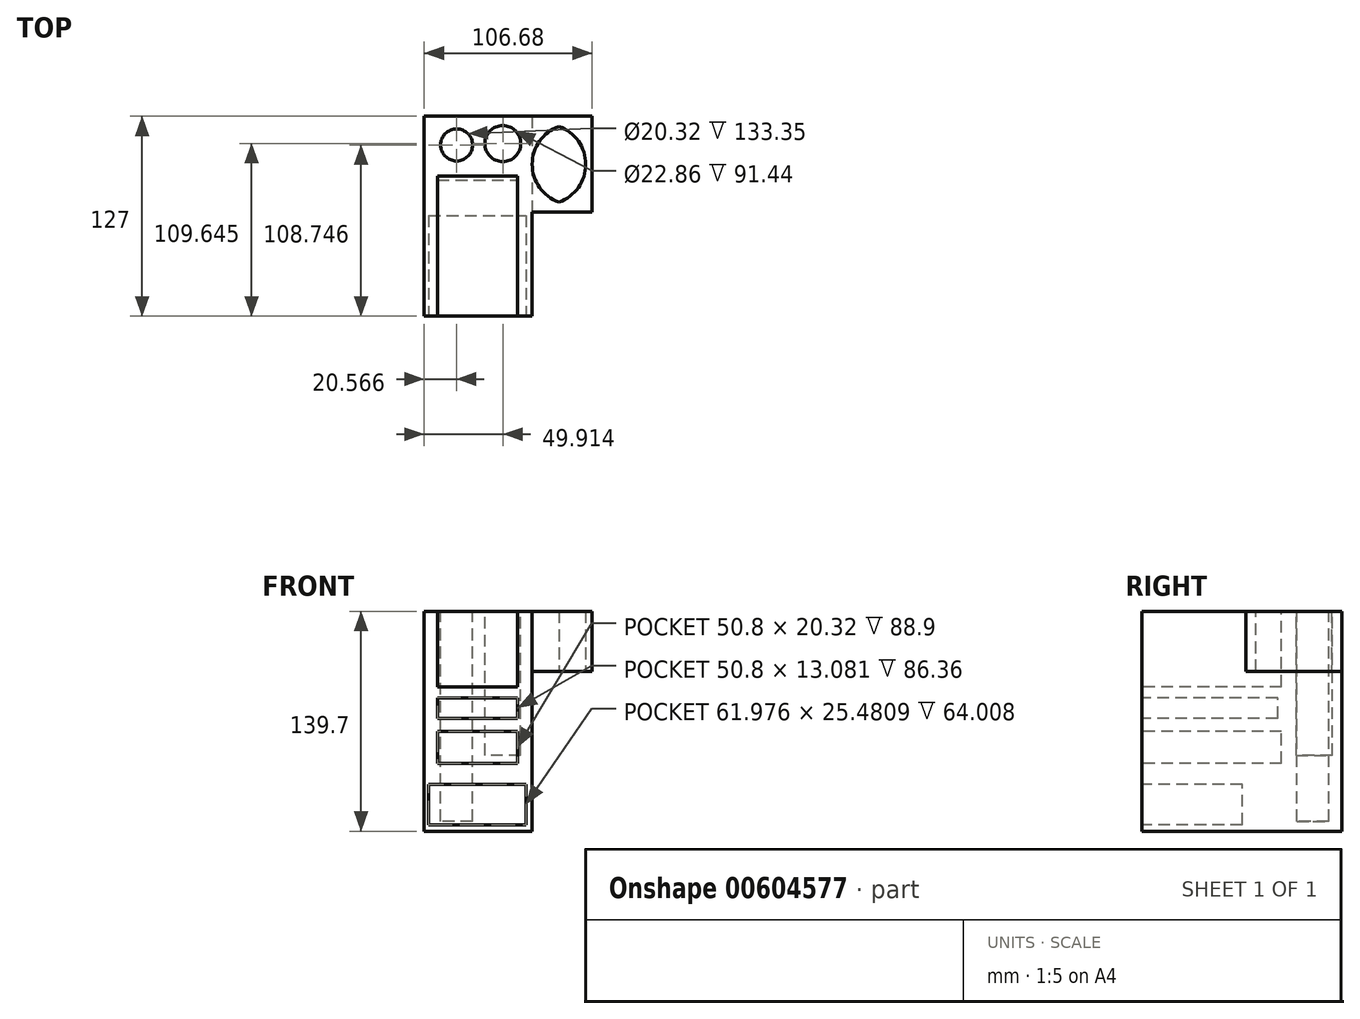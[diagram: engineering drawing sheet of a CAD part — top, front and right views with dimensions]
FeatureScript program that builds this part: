
annotation { "Feature Type Name" : "Feature", "Feature Type Description" : "" }
export const myFeature = defineFeature(function(context is Context, id is Id, definition is map)
    precondition{}
    {
        {
            var Q0;
            Q0=qCreatedBy(makeId("Top.planeOp"),FACE);
            var sketch = newSketch(context, id + "F0", { "sketchPlane" : qUnion([Q0])});
            skLineSegment(sketch, "E0.bottom", {"start": v(0, 0) * mm, "end": v(76.2, 0) * mm});
            skLineSegment(sketch, "E0.top", {"start": v(0, 127) * mm, "end": v(76.2, 127) * mm});
            skLineSegment(sketch, "E0.left", {"start": v(0, 0) * mm, "end": v(0, 127) * mm});
            skLineSegment(sketch, "E0.right", {"start": v(76.2, 0) * mm, "end": v(76.2, 127) * mm});
            skSolve(sketch);
        }
        {
            var Q0;
            Q0=makeQuery(id+"F0.imprint","IMPRINT",FACE,{"disambiguationData":[TD([[makeQuery(id+"F0.imprint","IMPRINT",EDGE,{"derivedFrom":sQuery(id+"F0.wireOp",EDGE,"E0.bottom")}),1.0]])]});
            extrude(context, id + "F1", {"entities" : qUnion([Q0]), "depth" : 139.7 * mm, "offsetDistance" : 25.4 * mm});
        }
        {
            var Q0;
            Q0=makeQuery(id+"F1.opExtrude","CAP_FACE",FACE,{"disambiguationData":[OSD([sQuery(id+"F0.wireOp",EDGE,"E0.bottom"),sQuery(id+"F0.wireOp",EDGE,"E0.top"),sQuery(id+"F0.wireOp",EDGE,"E0.left"),sQuery(id+"F0.wireOp",EDGE,"E0.right")])],"isStart":false});
            var sketch = newSketch(context, id + "F2", { "sketchPlane" : qUnion([Q0])});
            skCircle(sketch, "E1", {"center": v(18.57, 17.6) * mm, "radius": 11.43 * mm});
            skSolve(sketch);
        }
        {
            var Q0;
            Q0=makeQuery(id+"F2.imprint","IMPRINT",FACE,{"disambiguationData":[TD([[makeQuery(id+"F2.imprint","IMPRINT",EDGE,{"derivedFrom":sQuery(id+"F2.wireOp",EDGE,"E1")}),1.0]])]});
            extrude(context, id + "F3", {"entities" : qUnion([Q0]), "operationType" : NewBodyOperationType.REMOVE, "oppositeDirection" : true, "depth" : 91.44 * mm, "offsetDistance" : 25.4 * mm});
        }
        {
            var Q0;
            Q0=makeQuery(id+"F1.opExtrude","CAP_FACE",FACE,{"disambiguationData":[OSD([sQuery(id+"F0.wireOp",EDGE,"E0.bottom"),sQuery(id+"F0.wireOp",EDGE,"E0.top"),sQuery(id+"F0.wireOp",EDGE,"E0.left"),sQuery(id+"F0.wireOp",EDGE,"E0.right")])],"isStart":false});
            var sketch = newSketch(context, id + "F4", { "sketchPlane" : qUnion([Q0])});
            skCircle(sketch, "E2", {"center": v(20.57, 108.75) * mm, "radius": 10.16 * mm});
            skSolve(sketch);
        }
        {
            var Q0;
            Q0=makeQuery(id+"F4.imprint","IMPRINT",FACE,{"disambiguationData":[TD([[makeQuery(id+"F4.imprint","IMPRINT",EDGE,{"derivedFrom":sQuery(id+"F4.wireOp",EDGE,"E2")}),1.0]])]});
            extrude(context, id + "F5", {"entities" : qUnion([Q0]), "operationType" : NewBodyOperationType.REMOVE, "oppositeDirection" : true, "depth" : 133.35 * mm, "offsetDistance" : 25.4 * mm});
        }
        {
            var Q0;
            Q0=makeQuery(id+"F1.opExtrude","SWEPT_FACE",FACE,{"disambiguationData":[OSD([sQuery(id+"F0.wireOp",EDGE,"E0.right")])]});
            extrude(context, id + "F6", {"entities" : qUnion([Q0]), "operationType" : NewBodyOperationType.REMOVE, "oppositeDirection" : true, "depth" : 12.7 * mm, "offsetDistance" : 25.4 * mm});
        }
        {
            var Q0;
            Q0=makeQuery(id+"F1.opExtrude","SWEPT_FACE",FACE,{"disambiguationData":[OSD([sQuery(id+"F0.wireOp",EDGE,"E0.bottom")])]});
            var sketch = newSketch(context, id + "F7", { "sketchPlane" : qUnion([Q0])});
            skLineSegment(sketch, "E3.bottom", {"start": v(3.35, 4.2) * mm, "end": v(64.3, 4.2) * mm});
            skLineSegment(sketch, "E3.top", {"start": v(3.35, 29.68) * mm, "end": v(64.3, 29.68) * mm});
            skLineSegment(sketch, "E3.left", {"start": v(3.35, 4.2) * mm, "end": v(3.35, 29.68) * mm});
            skLineSegment(sketch, "E3.right", {"start": v(64.3, 4.2) * mm, "end": v(64.3, 29.68) * mm});
            skSolve(sketch);
        }
        {
            var Q0;
            Q0=makeQuery(id+"F6.boolean.opBoolean","COPY",FACE,{"derivedFrom":makeQuery(id+"F6.opExtrude","CAP_FACE",FACE,{"disambiguationData":[OSD([sQuery(id+"F0.wireOp",EDGE,"E0.right")])],"isStart":false})});
            extrude(context, id + "F8", {"entities" : qUnion([Q0]), "operationType" : NewBodyOperationType.ADD, "depth" : 5.08 * mm, "offsetDistance" : 25.4 * mm});
        }
        {
            var Q0;
            {var subQ0=sQuery(id+"F7.wireOp",EDGE,"E3.left");Q0=makeQuery(id+"F7.imprint","IMPRINT",FACE,{"disambiguationData":[TD([[makeQuery(id+"F7.imprint","IMPRINT",EDGE,{"derivedFrom":subQ0}),-1.0]])]});}
            var Q1;
            {var subQ0=sQuery(id+"F7.wireOp",EDGE,"E3.right");Q1=makeQuery(id+"F7.imprint","IMPRINT",FACE,{"disambiguationData":[TD([[makeQuery(id+"F7.imprint","IMPRINT",EDGE,{"derivedFrom":subQ0}),1.0]])]});}
            extrude(context, id + "F9", {"entities" : qUnion([Q0, Q1]), "operationType" : NewBodyOperationType.REMOVE, "oppositeDirection" : true, "depth" : 63.5 * mm, "offsetDistance" : 25.4 * mm});
        }
        {
            var Q0;
            Q0=makeQuery(id+"F3.boolean.opBoolean","COPY",FACE,{"derivedFrom":makeQuery(id+"F3.opExtrude","CAP_FACE",FACE,{"disambiguationData":[OSD([sQuery(id+"F2.wireOp",EDGE,"E1")])],"isStart":false})});
            extrude(context, id + "F10", {"entities" : qUnion([Q0]), "operationType" : NewBodyOperationType.ADD, "depth" : 91.44 * mm, "offsetDistance" : 25.4 * mm});
        }
        {
            var Q0;
            {var subQ0=sQuery(id+"F0.wireOp",EDGE,"E0.right");Q0=makeQuery(id+"F10.boolean.opBoolean","MERGE",FACE,{"derivedFrom":[makeQuery(id+"F8.boolean.opBoolean","MERGE",FACE,{"derivedFrom":[makeQuery(id+"F1.opExtrude","CAP_FACE",FACE,{"disambiguationData":[OSD([sQuery(id+"F0.wireOp",EDGE,"E0.bottom"),sQuery(id+"F0.wireOp",EDGE,"E0.top"),sQuery(id+"F0.wireOp",EDGE,"E0.left"),subQ0])],"isStart":false}),makeQuery(id+"F8.opExtrude","SWEPT_FACE",FACE,{"disambiguationData":[OSD([subQ0]),TDD([makeQuery(id+"F6.boolean.opBoolean","COPY",EDGE,{"derivedFrom":makeQuery(id+"F6.opExtrude","CAP_EDGE",EDGE,{"disambiguationData":[OSD([subQ0]),TDD([makeQuery(id+"F1.opExtrude","CAP_EDGE",EDGE,{"disambiguationData":[OSD([subQ0])],"isStart":false})])],"isStart":false})})])]})]}),makeQuery(id+"F10.opExtrude","CAP_FACE",FACE,{"disambiguationData":[OSD([sQuery(id+"F2.wireOp",EDGE,"E1")])],"isStart":false})]});}
            var sketch = newSketch(context, id + "F11", { "sketchPlane" : qUnion([Q0])});
            skCircle(sketch, "E4", {"center": v(49.91, 109.65) * mm, "radius": 11.43 * mm});
            skSolve(sketch);
        }
        {
            var Q0;
            Q0=makeQuery(id+"F11.imprint","IMPRINT",FACE,{"disambiguationData":[TD([[makeQuery(id+"F11.imprint","IMPRINT",EDGE,{"derivedFrom":sQuery(id+"F11.wireOp",EDGE,"E4")}),1.0]])]});
            extrude(context, id + "F12", {"entities" : qUnion([Q0]), "operationType" : NewBodyOperationType.REMOVE, "oppositeDirection" : true, "depth" : 91.44 * mm, "offsetDistance" : 25.4 * mm});
        }
        {
            var Q0;
            {var subQ0=sQuery(id+"F0.wireOp",EDGE,"E0.bottom");Q0=makeQuery(id+"F8.boolean.opBoolean","MERGE",FACE,{"derivedFrom":[makeQuery(id+"F1.opExtrude","SWEPT_FACE",FACE,{"disambiguationData":[OSD([subQ0])]}),makeQuery(id+"F8.opExtrude","SWEPT_FACE",FACE,{"disambiguationData":[OSD([subQ0,sQuery(id+"F0.wireOp",EDGE,"E0.right")])]})]});}
            var sketch = newSketch(context, id + "F13", { "sketchPlane" : qUnion([Q0])});
            skLineSegment(sketch, "E5.bottom", {"start": v(3.35, 43.16) * mm, "end": v(64.3, 43.16) * mm});
            skLineSegment(sketch, "E5.top", {"start": v(3.35, 63.48) * mm, "end": v(64.3, 63.48) * mm});
            skLineSegment(sketch, "E5.left", {"start": v(3.35, 43.16) * mm, "end": v(3.35, 63.48) * mm});
            skLineSegment(sketch, "E5.right", {"start": v(64.3, 43.16) * mm, "end": v(64.3, 63.48) * mm});
            skSolve(sketch);
        }
        {
            var Q0;
            Q0=makeQuery(id+"F13.imprint","IMPRINT",FACE,{"disambiguationData":[TD([[makeQuery(id+"F13.imprint","IMPRINT",EDGE,{"derivedFrom":sQuery(id+"F13.wireOp",EDGE,"E5.bottom")}),1.0]])]});
            extrude(context, id + "F14", {"entities" : qUnion([Q0]), "operationType" : NewBodyOperationType.REMOVE, "oppositeDirection" : true, "depth" : 88.9 * mm, "offsetDistance" : 25.4 * mm});
        }
        {
            var Q0;
            Q0=makeQuery(id+"F14.boolean.opBoolean","COPY",FACE,{"derivedFrom":makeQuery(id+"F14.opExtrude","SWEPT_FACE",FACE,{"disambiguationData":[OSD([sQuery(id+"F13.wireOp",EDGE,"E5.left")])]})});
            extrude(context, id + "F15", {"entities" : qUnion([Q0]), "operationType" : NewBodyOperationType.ADD, "depth" : 5.08 * mm, "offsetDistance" : 25.4 * mm});
        }
        {
            var Q0;
            Q0=makeQuery(id+"F14.boolean.opBoolean","COPY",FACE,{"derivedFrom":makeQuery(id+"F14.opExtrude","SWEPT_FACE",FACE,{"disambiguationData":[OSD([sQuery(id+"F13.wireOp",EDGE,"E5.right")])]})});
            extrude(context, id + "F16", {"entities" : qUnion([Q0]), "operationType" : NewBodyOperationType.ADD, "depth" : 5.08 * mm, "offsetDistance" : 25.4 * mm});
        }
        {
            var Q0;
            {var subQ0=sQuery(id+"F13.wireOp",EDGE,"E5.right");var subQ1=sQuery(id+"F13.wireOp",EDGE,"E5.left");var subQ2=sQuery(id+"F0.wireOp",EDGE,"E0.bottom");Q0=makeQuery(id+"F16.boolean.opBoolean","MERGE",FACE,{"derivedFrom":[makeQuery(id+"F15.boolean.opBoolean","MERGE",FACE,{"derivedFrom":[makeQuery(id+"F8.boolean.opBoolean","MERGE",FACE,{"derivedFrom":[makeQuery(id+"F1.opExtrude","SWEPT_FACE",FACE,{"disambiguationData":[OSD([subQ2])]}),makeQuery(id+"F8.opExtrude","SWEPT_FACE",FACE,{"disambiguationData":[OSD([subQ2,sQuery(id+"F0.wireOp",EDGE,"E0.right")])]})]}),makeQuery(id+"F15.opExtrude","SWEPT_FACE",FACE,{"disambiguationData":[OSD([subQ1]),TDD([makeQuery(id+"F14.boolean.opBoolean","COPY",EDGE,{"derivedFrom":makeQuery(id+"F14.opExtrude","CAP_EDGE",EDGE,{"disambiguationData":[OSD([subQ1])],"isStart":true})})])]})]}),makeQuery(id+"F16.opExtrude","SWEPT_FACE",FACE,{"disambiguationData":[OSD([subQ0]),TDD([makeQuery(id+"F14.boolean.opBoolean","COPY",EDGE,{"derivedFrom":makeQuery(id+"F14.opExtrude","CAP_EDGE",EDGE,{"disambiguationData":[OSD([subQ0])],"isStart":true})})])]})]});}
            var sketch = newSketch(context, id + "F17", { "sketchPlane" : qUnion([Q0])});
            skLineSegment(sketch, "E6.bottom", {"start": v(8.43, 71.79) * mm, "end": v(59.23, 71.79) * mm});
            skLineSegment(sketch, "E6.top", {"start": v(8.43, 84.49) * mm, "end": v(59.23, 84.49) * mm});
            skLineSegment(sketch, "E6.left", {"start": v(8.43, 71.79) * mm, "end": v(8.43, 84.49) * mm});
            skLineSegment(sketch, "E6.right", {"start": v(59.23, 71.79) * mm, "end": v(59.23, 84.49) * mm});
            skSolve(sketch);
        }
        {
            var Q0;
            Q0=makeQuery(id+"F17.imprint","IMPRINT",FACE,{"disambiguationData":[TD([[makeQuery(id+"F17.imprint","IMPRINT",EDGE,{"derivedFrom":sQuery(id+"F17.wireOp",EDGE,"E6.bottom")}),1.0]])]});
            extrude(context, id + "F18", {"entities" : qUnion([Q0]), "operationType" : NewBodyOperationType.REMOVE, "oppositeDirection" : true, "depth" : 86.36 * mm, "offsetDistance" : 25.4 * mm});
        }
        {
            var Q0;
            {var subQ0=sQuery(id+"F13.wireOp",EDGE,"E5.right");var subQ1=sQuery(id+"F13.wireOp",EDGE,"E5.left");var subQ2=sQuery(id+"F0.wireOp",EDGE,"E0.bottom");Q0=makeQuery(id+"F16.boolean.opBoolean","MERGE",FACE,{"derivedFrom":[makeQuery(id+"F15.boolean.opBoolean","MERGE",FACE,{"derivedFrom":[makeQuery(id+"F8.boolean.opBoolean","MERGE",FACE,{"derivedFrom":[makeQuery(id+"F1.opExtrude","SWEPT_FACE",FACE,{"disambiguationData":[OSD([subQ2])]}),makeQuery(id+"F8.opExtrude","SWEPT_FACE",FACE,{"disambiguationData":[OSD([subQ2,sQuery(id+"F0.wireOp",EDGE,"E0.right")])]})]}),makeQuery(id+"F15.opExtrude","SWEPT_FACE",FACE,{"disambiguationData":[OSD([subQ1]),TDD([makeQuery(id+"F14.boolean.opBoolean","COPY",EDGE,{"derivedFrom":makeQuery(id+"F14.opExtrude","CAP_EDGE",EDGE,{"disambiguationData":[OSD([subQ1])],"isStart":true})})])]})]}),makeQuery(id+"F16.opExtrude","SWEPT_FACE",FACE,{"disambiguationData":[OSD([subQ0]),TDD([makeQuery(id+"F14.boolean.opBoolean","COPY",EDGE,{"derivedFrom":makeQuery(id+"F14.opExtrude","CAP_EDGE",EDGE,{"disambiguationData":[OSD([subQ0])],"isStart":true})})])]})]});}
            var sketch = newSketch(context, id + "F19", { "sketchPlane" : qUnion([Q0])});
            skLineSegment(sketch, "E7.bottom", {"start": v(8.43, 91.68) * mm, "end": v(59.23, 91.68) * mm});
            skLineSegment(sketch, "E7.top", {"start": v(8.43, 139.7) * mm, "end": v(59.23, 139.7) * mm});
            skLineSegment(sketch, "E7.left", {"start": v(8.43, 91.68) * mm, "end": v(8.43, 139.7) * mm});
            skLineSegment(sketch, "E7.right", {"start": v(59.23, 91.68) * mm, "end": v(59.23, 139.7) * mm});
            skSolve(sketch);
        }
        {
            var Q0;
            Q0=makeQuery(id+"F19.imprint","IMPRINT",FACE,{"disambiguationData":[TD([[makeQuery(id+"F19.imprint","IMPRINT",EDGE,{"derivedFrom":sQuery(id+"F19.wireOp",EDGE,"E7.bottom")}),1.0]])]});
            extrude(context, id + "F20", {"entities" : qUnion([Q0]), "operationType" : NewBodyOperationType.REMOVE, "oppositeDirection" : true, "depth" : 88.9 * mm, "offsetDistance" : 25.4 * mm});
        }
        {
            var Q0;
            Q0=makeQuery(id+"F20.boolean.opBoolean","COPY",FACE,{"derivedFrom":makeQuery(id+"F20.opExtrude","SWEPT_FACE",FACE,{"disambiguationData":[OSD([sQuery(id+"F19.wireOp",EDGE,"E7.left")])]})});
            var sketch = newSketch(context, id + "F21", { "sketchPlane" : qUnion([Q0])});
            skLineSegment(sketch, "E8.bottom", {"start": v(0, 91.68) * mm, "end": v(6.76, 91.68) * mm});
            skLineSegment(sketch, "E8.top", {"start": v(0, 139.7) * mm, "end": v(6.76, 139.7) * mm});
            skLineSegment(sketch, "E8.left", {"start": v(0, 91.68) * mm, "end": v(0, 139.7) * mm});
            skLineSegment(sketch, "E8.right", {"start": v(6.76, 91.68) * mm, "end": v(6.76, 139.7) * mm});
            skSolve(sketch);
        }
        {
            var Q0;
            Q0=makeQuery(id+"F21.imprint","IMPRINT",FACE,{"disambiguationData":[TD([[makeQuery(id+"F21.imprint","IMPRINT",EDGE,{"derivedFrom":sQuery(id+"F21.wireOp",EDGE,"E8.bottom")}),-1.0]])]});
            extrude(context, id + "F22", {"entities" : qUnion([Q0]), "operationType" : NewBodyOperationType.ADD, "depth" : 55.88 * mm, "offsetDistance" : 25.4 * mm});
        }
        {
            var Q0;
            Q0=makeQuery(id+"F8.opExtrude","CAP_FACE",FACE,{"disambiguationData":[OSD([sQuery(id+"F0.wireOp",EDGE,"E0.right")])],"isStart":false});
            var sketch = newSketch(context, id + "F23", { "sketchPlane" : qUnion([Q0])});
            skLineSegment(sketch, "E9.bottom", {"start": v(127, 139.7) * mm, "end": v(66.04, 139.7) * mm});
            skLineSegment(sketch, "E9.top", {"start": v(127, 101.6) * mm, "end": v(66.04, 101.6) * mm});
            skLineSegment(sketch, "E9.left", {"start": v(127, 139.7) * mm, "end": v(127, 101.6) * mm});
            skLineSegment(sketch, "E9.right", {"start": v(66.04, 139.7) * mm, "end": v(66.04, 101.6) * mm});
            skSolve(sketch);
        }
        {
            var Q0;
            Q0=makeQuery(id+"F23.imprint","IMPRINT",FACE,{"disambiguationData":[TD([[makeQuery(id+"F23.imprint","IMPRINT",EDGE,{"derivedFrom":sQuery(id+"F23.wireOp",EDGE,"E9.bottom")}),-1.0]])]});
            extrude(context, id + "F24", {"entities" : qUnion([Q0]), "operationType" : NewBodyOperationType.ADD, "depth" : 38.1 * mm, "offsetDistance" : 25.4 * mm});
        }
        {
            var Q0;
            Q0=makeQuery(id+"F24.opExtrude","SWEPT_FACE",FACE,{"disambiguationData":[OSD([sQuery(id+"F23.wireOp",EDGE,"E9.top")])]});
            var sketch = newSketch(context, id + "F25", { "sketchPlane" : qUnion([Q0])});
            skLineSegment(sketch, "E10.bottom", {"start": v(68.58, -71.05) * mm, "end": v(102.6, -71.05) * mm});
            skLineSegment(sketch, "E10.top", {"start": v(68.58, -121.88) * mm, "end": v(102.6, -121.88) * mm});
            skLineSegment(sketch, "E10.left", {"start": v(68.58, -71.05) * mm, "end": v(68.58, -121.88) * mm});
            skLineSegment(sketch, "E10.right", {"start": v(102.6, -71.05) * mm, "end": v(102.6, -121.88) * mm});
            skSolve(sketch);
        }
        {
            var Q0;
            Q0=makeQuery(id+"F25.imprint","IMPRINT",FACE,{"disambiguationData":[TD([[makeQuery(id+"F25.imprint","IMPRINT",EDGE,{"derivedFrom":sQuery(id+"F25.wireOp",EDGE,"E10.bottom")}),-1.0]])]});
            extrude(context, id + "F26", {"entities" : qUnion([Q0]), "operationType" : NewBodyOperationType.REMOVE, "oppositeDirection" : true, "depth" : 50.8 * mm, "offsetDistance" : 25.4 * mm});
        }
        {
            var Q0;
            Q0=makeQuery(id+"F26.boolean.opBoolean","COPY",EDGE,{"derivedFrom":makeQuery(id+"F26.opExtrude","SWEPT_EDGE",EDGE,{"disambiguationData":[OSD([sQuery(id+"F25.wireOp",EDGE,"E10.bottom"),sQuery(id+"F25.wireOp",EDGE,"E10.right")])]})});
            var Q1;
            Q1=makeQuery(id+"F26.boolean.opBoolean","COPY",EDGE,{"derivedFrom":makeQuery(id+"F26.opExtrude","SWEPT_EDGE",EDGE,{"disambiguationData":[OSD([sQuery(id+"F25.wireOp",EDGE,"E10.top"),sQuery(id+"F25.wireOp",EDGE,"E10.right")])]})});
            var Q2;
            Q2=makeQuery(id+"F26.boolean.opBoolean","COPY",EDGE,{"derivedFrom":makeQuery(id+"F26.opExtrude","SWEPT_EDGE",EDGE,{"disambiguationData":[OSD([sQuery(id+"F23.wireOp",EDGE,"E9.top"),sQuery(id+"F25.wireOp",EDGE,"E10.bottom"),sQuery(id+"F25.wireOp",EDGE,"E10.left")])]})});
            var Q3;
            Q3=makeQuery(id+"F26.boolean.opBoolean","COPY",EDGE,{"derivedFrom":makeQuery(id+"F26.opExtrude","SWEPT_EDGE",EDGE,{"disambiguationData":[OSD([sQuery(id+"F23.wireOp",EDGE,"E9.top"),sQuery(id+"F25.wireOp",EDGE,"E10.top"),sQuery(id+"F25.wireOp",EDGE,"E10.left")])]})});
            fillet(context, id + "F27", {"entities" : qUnion([Q0, Q1, Q2, Q3]), "radius" : 25.4 * mm, "tangentPropagation" : true, "allowEdgeOverflow" : false});
        }
        {
            var Q0;
            Q0=makeQuery(id+"F9.boolean.opBoolean","COPY",FACE,{"derivedFrom":makeQuery(id+"F9.opExtrude","CAP_FACE",FACE,{"disambiguationData":[OSD([sQuery(id+"F7.wireOp",EDGE,"E3.bottom"),sQuery(id+"F7.wireOp",EDGE,"E3.top"),sQuery(id+"F7.wireOp",EDGE,"E3.left"),sQuery(id+"F7.wireOp",EDGE,"E3.right")])],"isStart":false})});
            extrude(context, id + "F28", {"entities" : qUnion([Q0]), "operationType" : NewBodyOperationType.REMOVE, "oppositeDirection" : true, "depth" : 0.5 * mm, "offsetDistance" : 25.4 * mm});
        }
        {
            var Q0;
            {var subQ0=sQuery(id+"F7.wireOp",EDGE,"E3.left");Q0=makeQuery(id+"F28.boolean.opBoolean","MERGE",FACE,{"derivedFrom":[makeQuery(id+"F9.boolean.opBoolean","COPY",FACE,{"derivedFrom":makeQuery(id+"F9.opExtrude","SWEPT_FACE",FACE,{"disambiguationData":[OSD([subQ0])]})}),makeQuery(id+"F28.opExtrude","SWEPT_FACE",FACE,{"disambiguationData":[OSD([subQ0])]})]});}
            extrude(context, id + "F29", {"entities" : qUnion([Q0]), "operationType" : NewBodyOperationType.REMOVE, "oppositeDirection" : true, "depth" : 0.5 * mm, "offsetDistance" : 25.4 * mm});
        }
        {
            var Q0;
            {var subQ0=sQuery(id+"F7.wireOp",EDGE,"E3.right");Q0=makeQuery(id+"F28.boolean.opBoolean","MERGE",FACE,{"derivedFrom":[makeQuery(id+"F9.boolean.opBoolean","COPY",FACE,{"derivedFrom":makeQuery(id+"F9.opExtrude","SWEPT_FACE",FACE,{"disambiguationData":[OSD([subQ0])]})}),makeQuery(id+"F28.opExtrude","SWEPT_FACE",FACE,{"disambiguationData":[OSD([subQ0])]})]});}
            extrude(context, id + "F30", {"entities" : qUnion([Q0]), "operationType" : NewBodyOperationType.REMOVE, "oppositeDirection" : true, "depth" : 0.5 * mm, "offsetDistance" : 25.4 * mm});
        }
        {
            var Q0;
            Q0=makeQuery(id+"F18.boolean.opBoolean","COPY",FACE,{"derivedFrom":makeQuery(id+"F18.opExtrude","SWEPT_FACE",FACE,{"disambiguationData":[OSD([sQuery(id+"F17.wireOp",EDGE,"E6.top")])]})});
            extrude(context, id + "F31", {"entities" : qUnion([Q0]), "operationType" : NewBodyOperationType.REMOVE, "oppositeDirection" : true, "depth" : 0.38 * mm, "offsetDistance" : 25.4 * mm});
        }
        {
            var Q0;
            Q0=makeQuery(id+"F22.opExtrude","SWEPT_FACE",FACE,{"disambiguationData":[OSD([sQuery(id+"F21.wireOp",EDGE,"E8.right")])]});
            extrude(context, id + "F32", {"entities" : qUnion([Q0]), "operationType" : NewBodyOperationType.REMOVE, "oppositeDirection" : true, "depth" : 25.4 * mm, "offsetDistance" : 25.4 * mm});
        }
    });
